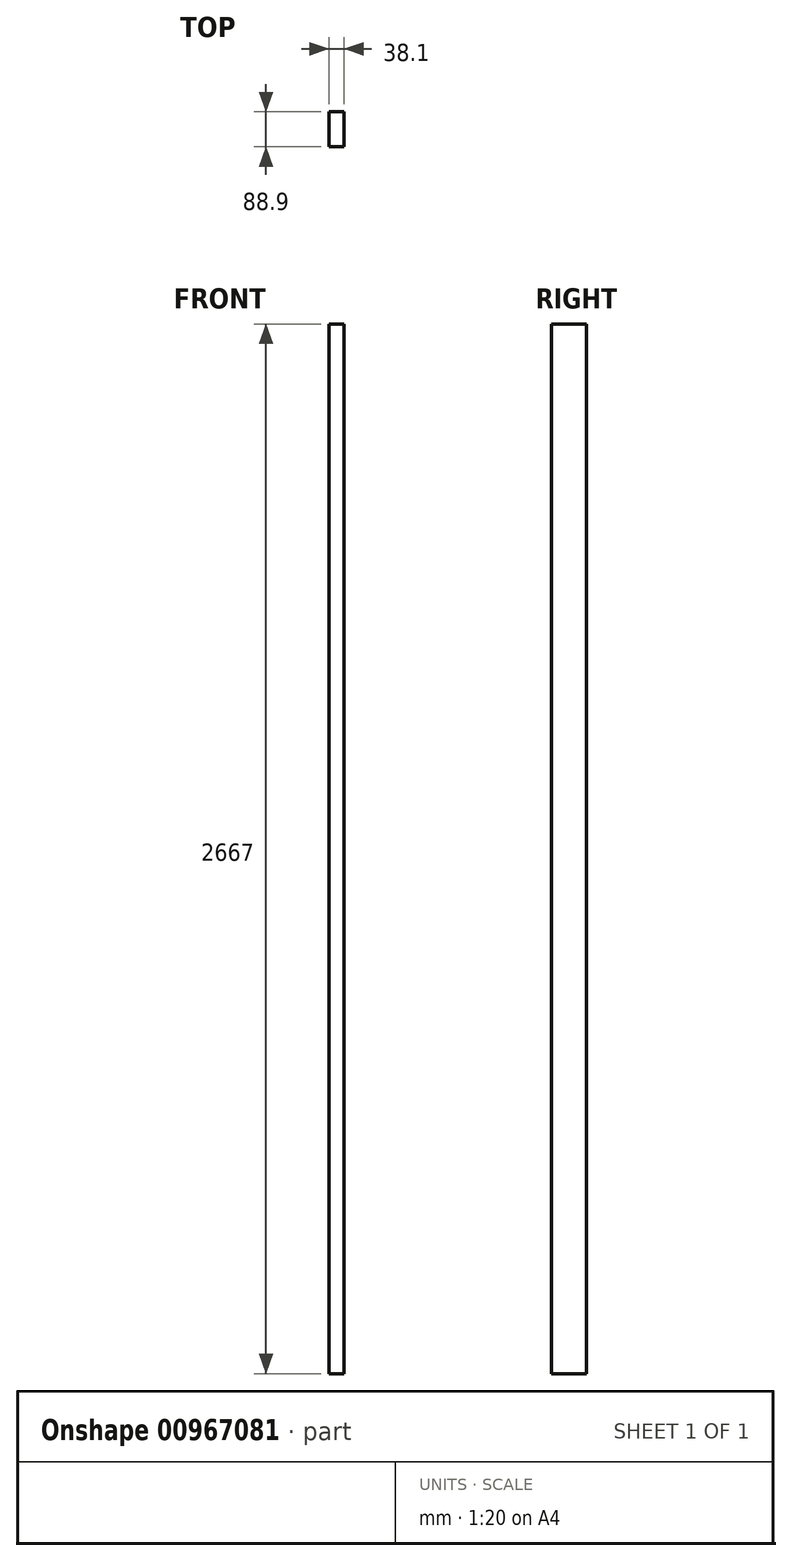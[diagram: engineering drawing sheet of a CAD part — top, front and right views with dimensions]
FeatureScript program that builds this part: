
annotation { "Feature Type Name" : "Feature", "Feature Type Description" : "" }
export const myFeature = defineFeature(function(context is Context, id is Id, definition is map)
    precondition{}
    {
        {
            var Q0;
            Q0=qCreatedBy(makeId("Top.planeOp"),FACE);
            var sketch = newSketch(context, id + "F0", { "sketchPlane" : qUnion([Q0])});
            skLineSegment(sketch, "E0.bottom", {"start": v(0, 0) * mm, "end": v(38.1, 0) * mm});
            skLineSegment(sketch, "E0.top", {"start": v(0, 88.9) * mm, "end": v(38.1, 88.9) * mm});
            skLineSegment(sketch, "E0.left", {"start": v(0, 0) * mm, "end": v(0, 88.9) * mm});
            skLineSegment(sketch, "E0.right", {"start": v(38.1, 0) * mm, "end": v(38.1, 88.9) * mm});
            skSolve(sketch);
        }
        {
            var Q0;
            Q0 = qSketchRegion(id + "F0", true);
            extrude(context, id + "F1", {"entities" : qUnion([Q0]), "depth" : 2667 * mm, "offsetDistance" : 25.4 * mm});
        }
    });
